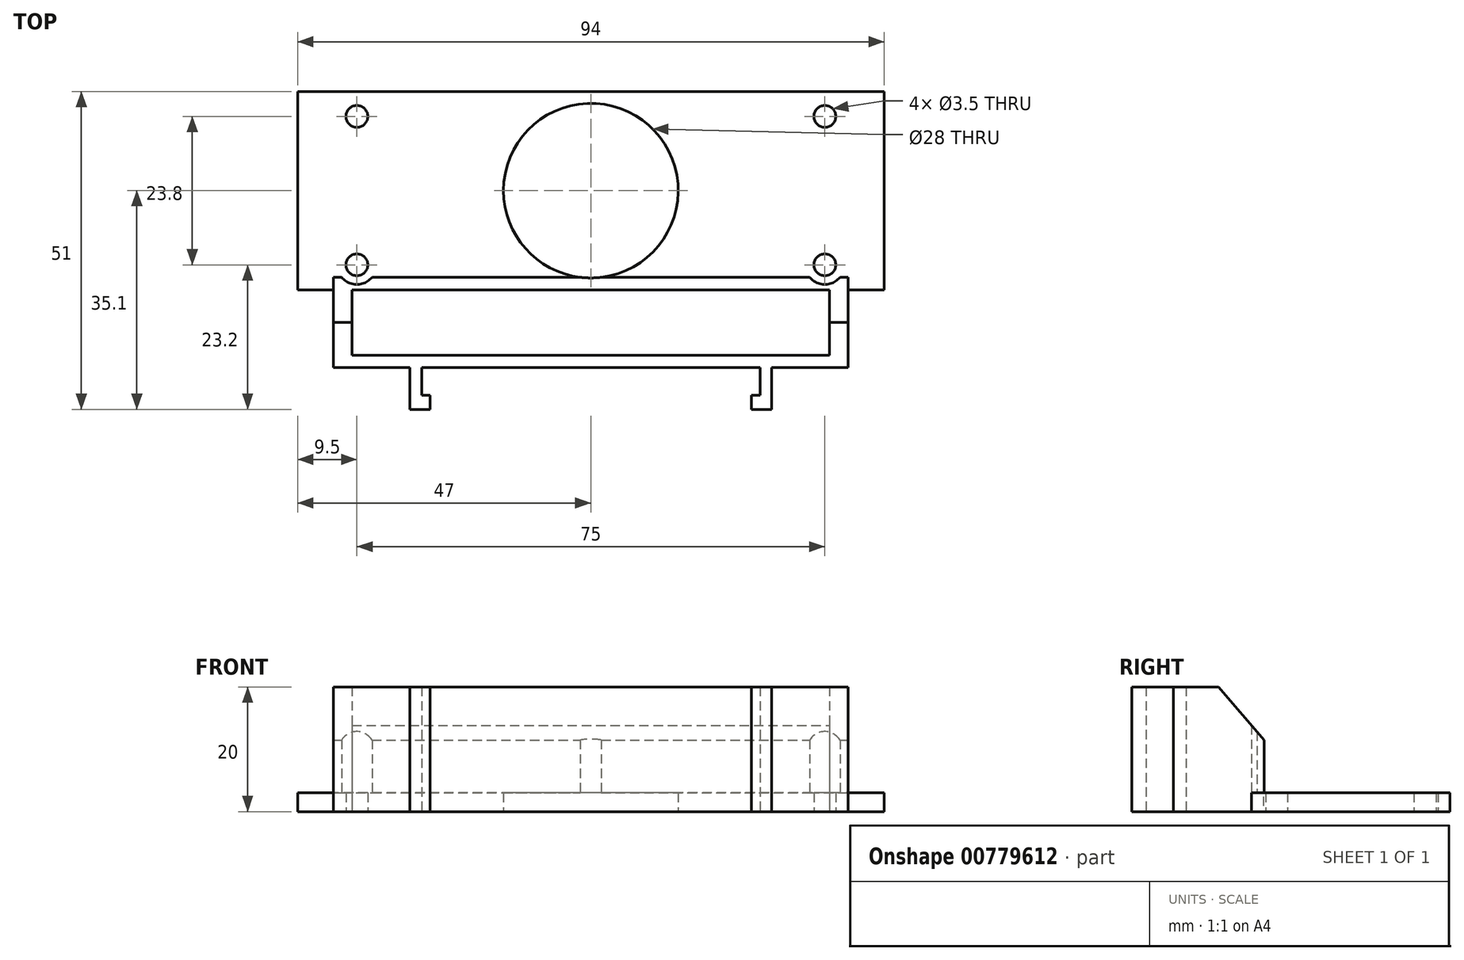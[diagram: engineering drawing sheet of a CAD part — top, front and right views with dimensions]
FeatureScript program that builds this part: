
annotation { "Feature Type Name" : "Feature", "Feature Type Description" : "" }
export const myFeature = defineFeature(function(context is Context, id is Id, definition is map)
    precondition{}
    {
        {
            var Q0;
            Q0=qCreatedBy(makeId("Top.planeOp"),FACE);
            var sketch = newSketch(context, id + "F0", { "sketchPlane" : qUnion([Q0])});
            skLineSegment(sketch, "E0.bottom", {"start": v(47, 15.9) * mm, "end": v(-47, 15.9) * mm});
            skLineSegment(sketch, "E0.top", {"start": v(47, -15.9) * mm, "end": v(-47, -15.9) * mm});
            skLineSegment(sketch, "E0.left", {"start": v(47, 15.9) * mm, "end": v(47, -15.9) * mm});
            skLineSegment(sketch, "E0.right", {"start": v(-47, 15.9) * mm, "end": v(-47, -15.9) * mm});
            skPoint(sketch, "E0.middle", {"position": v(0, 0) * mm});
            skCircle(sketch, "E1", {"center": v(-37.5, 11.9) * mm, "radius": 1.75 * mm});
            skCircle(sketch, "E2", {"center": v(-37.5, -11.9) * mm, "radius": 1.75 * mm});
            skCircle(sketch, "E3", {"center": v(37.5, -11.9) * mm, "radius": 1.75 * mm});
            skCircle(sketch, "E4", {"center": v(37.5, 11.9) * mm, "radius": 1.75 * mm});
            skSolve(sketch);
        }
        {
            var Q0;
            Q0=qSketchRegion(id+"F0",true);
            extrude(context, id + "F1", {"entities" : qUnion([Q0]), "depth" : 3 * mm, "offsetDistance" : 25 * mm});
        }
        {
            var Q0;
            Q0=qCreatedBy(makeId("Top.planeOp"),FACE);
            var sketch = newSketch(context, id + "F2", { "sketchPlane" : qUnion([Q0])});
            skLineSegment(sketch, "E5.bottom", {"start": v(38.25, -15.9) * mm, "end": v(-38.25, -15.9) * mm});
            skLineSegment(sketch, "E5.top", {"start": v(38.25, -26.4) * mm, "end": v(-38.25, -26.4) * mm});
            skLineSegment(sketch, "E5.left", {"start": v(38.25, -15.9) * mm, "end": v(38.25, -26.4) * mm});
            skLineSegment(sketch, "E5.right", {"start": v(-38.25, -15.9) * mm, "end": v(-38.25, -26.4) * mm});
            skPoint(sketch, "E5.middle", {"position": v(0, -21.15) * mm});
            skLineSegment(sketch, "E6.0", {"start": v(41.25, -13.9) * mm, "end": v(-41.25, -13.9) * mm});
            skLineSegment(sketch, "E6.2", {"start": v(41.25, -28.4) * mm, "end": v(-41.25, -28.4) * mm});
            skLineSegment(sketch, "E7.0", {"start": v(47, -15.9) * mm, "end": v(-47, -15.9) * mm, "construction": true});
            skLineSegment(sketch, "E8", {"start": v(41.25, -13.9) * mm, "end": v(41.25, -28.4) * mm});
            skLineSegment(sketch, "E9", {"start": v(-41.25, -13.9) * mm, "end": v(-41.25, -28.4) * mm});
            skLineSegment(sketch, "E10", {"start": v(29, -28.4) * mm, "end": v(29, -35.1) * mm});
            skLineSegment(sketch, "E11", {"start": v(29, -35.1) * mm, "end": v(25.75, -35.1) * mm});
            skLineSegment(sketch, "E12", {"start": v(25.75, -35.1) * mm, "end": v(25.75, -32.8) * mm});
            skLineSegment(sketch, "E13", {"start": v(25.75, -32.8) * mm, "end": v(27.1, -32.8) * mm});
            skLineSegment(sketch, "E14", {"start": v(27.1, -32.8) * mm, "end": v(27.1, -28.4) * mm});
            skLineSegment(sketch, "E15.MirrorCS", {"start": v(-29, -28.4) * mm, "end": v(-29, -35.1) * mm});
            skLineSegment(sketch, "E16.MirrorCS", {"start": v(-27.1, -32.8) * mm, "end": v(-27.1, -28.4) * mm});
            skLineSegment(sketch, "E17.MirrorCS", {"start": v(-25.75, -32.8) * mm, "end": v(-27.1, -32.8) * mm});
            skLineSegment(sketch, "E18.MirrorCS", {"start": v(-25.75, -35.1) * mm, "end": v(-25.75, -32.8) * mm});
            skLineSegment(sketch, "E19.MirrorCS", {"start": v(-29, -35.1) * mm, "end": v(-25.75, -35.1) * mm});
            skSolve(sketch);
        }
        {
            var Q0;
            Q0=makeQuery(id+"F2.imprint","IMPRINT",FACE,{"disambiguationData":[TD([[makeQuery(id+"F2.imprint","IMPRINT",EDGE,{"derivedFrom":sQuery(id+"F2.wireOp",EDGE,"E5.bottom")}),-1.0]])]});
            var Q1;
            {var subQ0=sQuery(id+"F2.wireOp",EDGE,"E15.MirrorCS");Q1=makeQuery(id+"F2.imprint","IMPRINT",FACE,{"disambiguationData":[TD([[makeQuery(id+"F2.imprint","IMPRINT",EDGE,{"derivedFrom":subQ0}),1.0]])]});}
            var Q2;
            {var subQ0=sQuery(id+"F2.wireOp",EDGE,"E10");Q2=makeQuery(id+"F2.imprint","IMPRINT",FACE,{"disambiguationData":[TD([[makeQuery(id+"F2.imprint","IMPRINT",EDGE,{"derivedFrom":subQ0}),-1.0]])]});}
            extrude(context, id + "F3", {"entities" : qUnion([Q0, Q1, Q2]), "operationType" : NewBodyOperationType.ADD, "depth" : 20 * mm, "offsetDistance" : 25 * mm});
        }
        {
            var Q0;
            Q0=makeQuery(id+"F3.opExtrude","SWEPT_FACE",FACE,{"disambiguationData":[OSD([sQuery(id+"F2.wireOp",EDGE,"E8")])]});
            var sketch = newSketch(context, id + "F4", { "sketchPlane" : qUnion([Q0])});
            skLineSegment(sketch, "E20.0", {"start": v(-13.9, 20) * mm, "end": v(-13.9, 3) * mm});
            skLineSegment(sketch, "E21", {"start": v(-21.15, 20) * mm, "end": v(-13.9, 11.5) * mm});
            skSolve(sketch);
        }
        {
            var Q0;
            {var subQ3=sQuery(id+"F4.wireOp",EDGE,"E21");Q0=makeQuery(id+"F4.imprint","IMPRINT",FACE,{"disambiguationData":[TD([[makeQuery(id+"F4.imprint","IMPRINT",EDGE,{"derivedFrom":subQ3}),1.0]])]});}
            var Q1;
            Q1=makeQuery(id+"F3.opExtrude","SWEPT_FACE",FACE,{"disambiguationData":[OSD([sQuery(id+"F2.wireOp",EDGE,"E9")])]});
            extrude(context, id + "F5", {"entities" : qUnion([Q0]), "operationType" : NewBodyOperationType.REMOVE, "endBound" : BoundingType.UP_TO_SURFACE, "oppositeDirection" : true, "depth" : 25 * mm, "endBoundEntityFace" : qUnion([Q1]), "offsetDistance" : 25 * mm});
        }
        {
            var Q0;
            Q0=makeQuery(id+"F3.boolean.opBoolean","MERGE",FACE,{"derivedFrom":[makeQuery(id+"F1.opExtrude","CAP_FACE",FACE,{"disambiguationData":[OSD([sQuery(id+"F0.wireOp",EDGE,"E0.bottom"),sQuery(id+"F0.wireOp",EDGE,"E0.top"),sQuery(id+"F0.wireOp",EDGE,"E0.left"),sQuery(id+"F0.wireOp",EDGE,"E0.right"),sQuery(id+"F0.wireOp",EDGE,"E1"),sQuery(id+"F0.wireOp",EDGE,"E2"),sQuery(id+"F0.wireOp",EDGE,"E3"),sQuery(id+"F0.wireOp",EDGE,"E4")])],"isStart":true}),makeQuery(id+"F3.opExtrude","CAP_FACE",FACE,{"disambiguationData":[OSD([sQuery(id+"F2.wireOp",EDGE,"E5.bottom"),sQuery(id+"F2.wireOp",EDGE,"E5.top"),sQuery(id+"F2.wireOp",EDGE,"E5.left"),sQuery(id+"F2.wireOp",EDGE,"E5.right"),sQuery(id+"F2.wireOp",EDGE,"E6.0"),sQuery(id+"F2.wireOp",EDGE,"E6.1"),sQuery(id+"F2.wireOp",EDGE,"E6.2"),sQuery(id+"F2.wireOp",EDGE,"E6.3")])],"isStart":true})]});
            var sketch = newSketch(context, id + "F6", { "sketchPlane" : qUnion([Q0])});
            skCircle(sketch, "E22", {"center": v(0, 0) * mm, "radius": 14 * mm});
            skSolve(sketch);
        }
        {
            var Q0;
            Q0=qSketchRegion(id+"F6",true);
            extrude(context, id + "F7", {"entities" : qUnion([Q0]), "operationType" : NewBodyOperationType.REMOVE, "oppositeDirection" : true, "depth" : 25 * mm, "offsetDistance" : 25 * mm});
        }
        {
            var Q0;
            Q0=makeQuery(id+"F1.opExtrude","CAP_FACE",FACE,{"disambiguationData":[OSD([sQuery(id+"F0.wireOp",EDGE,"E0.bottom"),sQuery(id+"F0.wireOp",EDGE,"E0.top"),sQuery(id+"F0.wireOp",EDGE,"E0.left"),sQuery(id+"F0.wireOp",EDGE,"E0.right"),sQuery(id+"F0.wireOp",EDGE,"E1"),sQuery(id+"F0.wireOp",EDGE,"E2"),sQuery(id+"F0.wireOp",EDGE,"E3"),sQuery(id+"F0.wireOp",EDGE,"E4")])],"isStart":false});
            var sketch = newSketch(context, id + "F8", { "sketchPlane" : qUnion([Q0])});
            skCircle(sketch, "E23.0", {"center": v(37.5, -11.9) * mm, "radius": 3.15 * mm});
            skCircle(sketch, "E24.0", {"center": v(-37.5, -11.9) * mm, "radius": 3.15 * mm});
            skSolve(sketch);
        }
        {
            var Q0;
            Q0=qSketchRegion(id+"F8",true);
            extrude(context, id + "F9", {"entities" : qUnion([Q0]), "operationType" : NewBodyOperationType.REMOVE, "depth" : 25 * mm, "offsetDistance" : 25 * mm});
        }
    });
